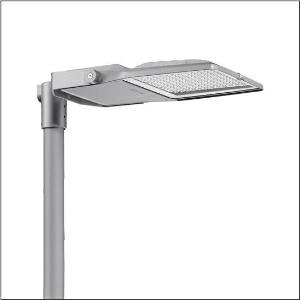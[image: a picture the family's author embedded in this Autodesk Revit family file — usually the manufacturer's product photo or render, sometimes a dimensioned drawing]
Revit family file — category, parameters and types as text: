
# Revit family: floodlight_fl_21_midi___pl52_5xa7786f2d3a_9b56
name_source: partatom
category: Lighting Fixtures
units: mm (PartAtom-declared; Revit-internal decimal feet)

## family parameters
Cut with Voids When Loaded = No
Host = Face
Light Source = No
Part Type = Normal
Room Calculation Point = No
Round Connector Dimension = Use Diameter
Shared = No

## types (1)
- --- (1 x LED, 35750 lm, 271.6 W, 3000K)
    Apparent Load = 272 VA
    CIE Flux Codes = 26 60 98 100 100
    Color Rendering = 70
    Color Temperature = 3000K
    Default Elevation = 1800 mm
    Description = Floodlight FL 21 midi, floodlight, primary light control with lens, of PMMA, primary optical cover: protective disc, of toughened safety glass, transparent, light distribution: PL52, light emission: direct distribution, installation type: surface-mounted, LED, High Power LED, rated luminous flux: 35.750lm, luminous efficacy: 132lm/W, light colour: 730, colour temperature: 3000K, control gear: ECG Smart Interface, control: flexible luminous flux parameterisation, time-dependent luminous flux control, constant luminous flux control, overheat protection, presetting dimming logarithmic, with terminal, 6-pole, mains connection: 220..240V, AC, 50/60Hz, start of lifetime: 272W, end of service life: 287W, reduction: 123W, luminaire housing, of diecast aluminium, powder-coated, Siteco® metallic grey (DB 702S), corrosivity category C5 mid according to DIN EN ISO 12944, sealing non-destructively replaceable, please order mast flange separately, mast bracket, of steel, galvanised, powder-coated, Siteco® metallic grey (DB 702S), Smart Interface below and above, protection rating (complete): IP66, insulation class (complete): insulation class II (safety insulation), certification: CE, protection symbol: D, impact resistance: IK08, permissible operating ambient temperature: -40..+40°C, permissible operating ambient temperature for outdoor applications: -40..+50°C, standard: DIN EN 12944, LABS conformity tested according to VDMA 24364:2018-05, packaging unit: 1 piece

Light Distribution: PL52
    Height = 76 mm
    Lamp = 1 x LED
    Lamp Light Flux = 35750 lm
    Lamp Power = 271.6 W
    Lamp count = 1
    Length = 657 mm
    Luminous efficacy = 132 lm/W
    Manufacturer = Siteco
    ModVariant = No
    Model = 5XA7786F2D3A
    Number of Poles = 1
    OnlyDefault = Yes
    Power Factor = 1
    Product Name = Floodlight FL 21 midi | PL52
    Product group = floodlight | pylon annexe
    ProductGroupID = 6200
    Protection Class = Protection class II
    Protection Degree = IP 66
    RLX_Detail_Level = 1
    RLX_Emergency_Light_Flux = 0 lm
    RLX_Emergency_Type = 0
    RLX_Emergency_Type_DB = No
    RlxData = <blob elided: 153793 chars, md5=92c3a3b0>
    Socket = socket
    Standby Power = 0 W
    System Light Flux = 35750 lm
    System Power = 272 W
    Type Comments = factory setting: luminous flux: 100 % | dim-lin: 254 | 620 mA
    Type Image = l_1007123.jpg
    URL = http://relux.com
    VarID = @adj_128587
    Voltage = 0 V
    Weight = 0.00 kg
    Width = 442 mm

## geometry (parser evidence)
native form markers: Blend x4, Sweep x12
no freeform markers — native parametric forms only
